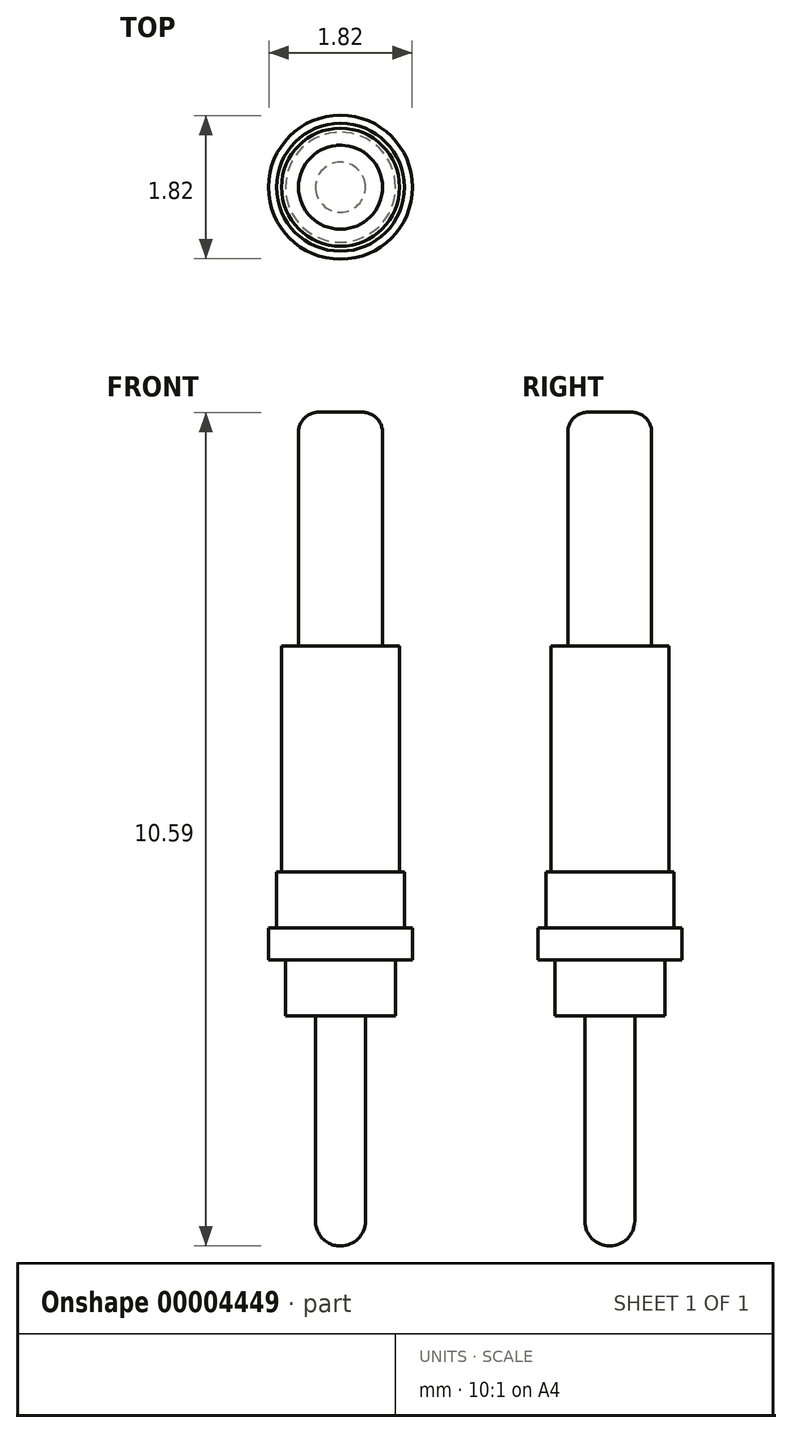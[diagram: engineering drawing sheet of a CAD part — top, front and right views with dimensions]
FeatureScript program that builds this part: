
annotation { "Feature Type Name" : "Feature", "Feature Type Description" : "" }
export const myFeature = defineFeature(function(context is Context, id is Id, definition is map)
    precondition{}
    {
        {
            var Q0;
            Q0=qCreatedBy(makeId("Top.planeOp"),FACE);
            var sketch = newSketch(context, id + "F0", { "sketchPlane" : qUnion([Q0])});
            skCircle(sketch, "E0", {"center": v(0, 0) * mm, "radius": 0.7 * mm});
            skSolve(sketch);
        }
        {
            var Q0;
            Q0=makeQuery(id+"F0.imprint","IMPRINT",FACE,{"disambiguationData":[TD([[makeQuery(id+"F0.imprint","IMPRINT",EDGE,{"derivedFrom":sQuery(id+"F0.wireOp",EDGE,"E0")}),1.0]])]});
            extrude(context, id + "F1", {"entities" : qUnion([Q0]), "depth" : 0.71 * mm});
        }
        {
            var Q0;
            Q0=makeQuery(id+"F1.opExtrude","CAP_FACE",FACE,{"disambiguationData":[OSD([sQuery(id+"F0.wireOp",EDGE,"E0")])],"isStart":false});
            var sketch = newSketch(context, id + "F2", { "sketchPlane" : qUnion([Q0])});
            skCircle(sketch, "E1", {"center": v(0, 0) * mm, "radius": 0.91 * mm});
            skSolve(sketch);
        }
        {
            var Q0;
            {var subQ0=makeQuery(id+"F2.imprint","IMPRINT",EDGE,{"derivedFrom":makeQuery(id+"F1.opExtrude","CAP_EDGE",EDGE,{"disambiguationData":[OSD([sQuery(id+"F0.wireOp",EDGE,"E0")])],"isStart":false})});Q0=qUnion([makeQuery(id+"F2.imprint","IMPRINT",FACE,{"disambiguationData":[TD([[makeQuery(id+"F2.imprint","IMPRINT",EDGE,{"derivedFrom":sQuery(id+"F2.wireOp",EDGE,"E1")}),1.0]])]}),makeQuery(id+"F2.imprint","IMPRINT",FACE,{"disambiguationData":[TD([[subQ0,1.0]])]})]);}
            extrude(context, id + "F3", {"entities" : qUnion([Q0]), "operationType" : NewBodyOperationType.ADD, "depth" : 0.4 * mm});
        }
        {
            var Q0;
            Q0=makeQuery(id+"F3.opExtrude","CAP_FACE",FACE,{"disambiguationData":[OSD([sQuery(id+"F2.wireOp",EDGE,"E1")])],"isStart":false});
            var sketch = newSketch(context, id + "F4", { "sketchPlane" : qUnion([Q0])});
            skCircle(sketch, "E2", {"center": v(0, 0) * mm, "radius": 0.81 * mm});
            skSolve(sketch);
        }
        {
            var Q0;
            Q0=makeQuery(id+"F4.imprint","IMPRINT",FACE,{"disambiguationData":[TD([[makeQuery(id+"F4.imprint","IMPRINT",EDGE,{"derivedFrom":sQuery(id+"F4.wireOp",EDGE,"E2")}),1.0]])]});
            extrude(context, id + "F5", {"entities" : qUnion([Q0]), "operationType" : NewBodyOperationType.ADD, "depth" : 0.71 * mm});
        }
        {
            var Q0;
            Q0=makeQuery(id+"F5.opExtrude","CAP_FACE",FACE,{"disambiguationData":[OSD([sQuery(id+"F4.wireOp",EDGE,"E2")])],"isStart":false});
            var sketch = newSketch(context, id + "F6", { "sketchPlane" : qUnion([Q0])});
            skCircle(sketch, "E3", {"center": v(0, 0) * mm, "radius": 0.75 * mm});
            skSolve(sketch);
        }
        {
            var Q0;
            Q0=makeQuery(id+"F6.imprint","IMPRINT",FACE,{"disambiguationData":[TD([[makeQuery(id+"F6.imprint","IMPRINT",EDGE,{"derivedFrom":sQuery(id+"F6.wireOp",EDGE,"E3")}),1.0]])]});
            extrude(context, id + "F7", {"entities" : qUnion([Q0]), "operationType" : NewBodyOperationType.ADD, "depth" : 2.87 * mm});
        }
        {
            var Q0;
            Q0=makeQuery(id+"F7.opExtrude","CAP_FACE",FACE,{"disambiguationData":[OSD([sQuery(id+"F6.wireOp",EDGE,"E3")])],"isStart":false});
            var sketch = newSketch(context, id + "F8", { "sketchPlane" : qUnion([Q0])});
            skCircle(sketch, "E4", {"center": v(0, 0) * mm, "radius": 0.53 * mm});
            skSolve(sketch);
        }
        {
            var Q0;
            Q0=makeQuery(id+"F8.imprint","IMPRINT",FACE,{"disambiguationData":[TD([[makeQuery(id+"F8.imprint","IMPRINT",EDGE,{"derivedFrom":sQuery(id+"F8.wireOp",EDGE,"E4")}),1.0]])]});
            extrude(context, id + "F9", {"entities" : qUnion([Q0]), "operationType" : NewBodyOperationType.ADD, "depth" : 2.97 * mm});
        }
        {
            var Q0;
            Q0=makeQuery(id+"F1.opExtrude","CAP_FACE",FACE,{"disambiguationData":[OSD([sQuery(id+"F0.wireOp",EDGE,"E0")])],"isStart":true});
            var sketch = newSketch(context, id + "F10", { "sketchPlane" : qUnion([Q0])});
            skCircle(sketch, "E5", {"center": v(0, 0) * mm, "radius": 0.32 * mm});
            skSolve(sketch);
        }
        {
            var Q0;
            Q0=makeQuery(id+"F10.imprint","IMPRINT",FACE,{"disambiguationData":[TD([[makeQuery(id+"F10.imprint","IMPRINT",EDGE,{"derivedFrom":sQuery(id+"F10.wireOp",EDGE,"E5")}),1.0]])]});
            extrude(context, id + "F11", {"entities" : qUnion([Q0]), "operationType" : NewBodyOperationType.ADD, "depth" : 2.92 * mm});
        }
        {
            var Q0;
            Q0=makeQuery(id+"F11.opExtrude","CAP_EDGE",EDGE,{"disambiguationData":[OSD([sQuery(id+"F10.wireOp",EDGE,"E5")])],"isStart":false});
            fillet(context, id + "F12", {"entities" : qUnion([Q0]), "radius" : 0.32 * mm, "tangentPropagation" : true, "allowEdgeOverflow" : false});
        }
        {
            var Q0;
            Q0=makeQuery(id+"F7.opExtrude","CAP_FACE",FACE,{"disambiguationData":[OSD([sQuery(id+"F6.wireOp",EDGE,"E3")])],"isStart":false});
            var sketch = newSketch(context, id + "F13", { "sketchPlane" : qUnion([Q0])});
            skCircle(sketch, "E6", {"center": v(0, 0) * mm, "radius": 0.54 * mm});
            skSolve(sketch);
        }
        {
            var Q0;
            {var subQ0=makeQuery(id+"F13.imprint","IMPRINT",EDGE,{"derivedFrom":makeQuery(id+"F9.opExtrude","CAP_EDGE",EDGE,{"disambiguationData":[OSD([sQuery(id+"F8.wireOp",EDGE,"E4")])],"isStart":true})});Q0=qUnion([makeQuery(id+"F13.imprint","IMPRINT",FACE,{"disambiguationData":[TD([[subQ0,1.0]])]}),makeQuery(id+"F13.imprint","IMPRINT",FACE,{"disambiguationData":[TD([[makeQuery(id+"F13.imprint","IMPRINT",EDGE,{"derivedFrom":sQuery(id+"F13.wireOp",EDGE,"E6")}),1.0]])]})]);}
            extrude(context, id + "F14", {"entities" : qUnion([Q0]), "operationType" : NewBodyOperationType.ADD, "depth" : 0.69 * mm});
        }
        {
            var Q0;
            Q0=makeQuery(id+"F9.opExtrude","CAP_FACE",FACE,{"disambiguationData":[OSD([sQuery(id+"F8.wireOp",EDGE,"E4")])],"isStart":false});
            fillet(context, id + "F15", {"entities" : qUnion([Q0]), "radius" : 0.25 * mm, "tangentPropagation" : true, "allowEdgeOverflow" : false});
        }
    });
